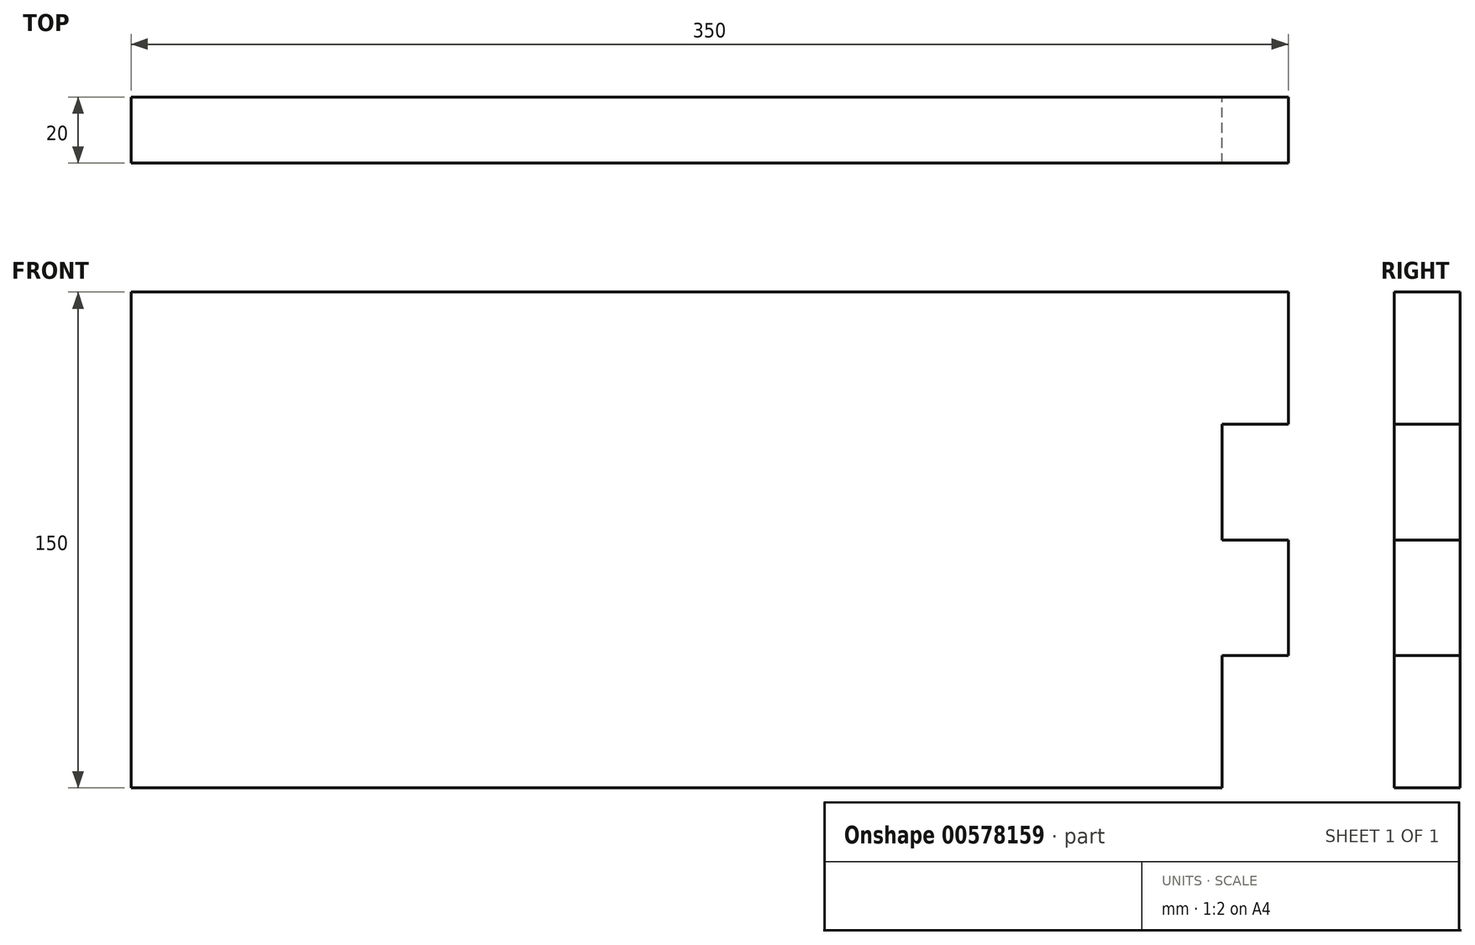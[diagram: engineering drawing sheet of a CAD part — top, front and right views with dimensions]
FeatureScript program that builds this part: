
annotation { "Feature Type Name" : "Feature", "Feature Type Description" : "" }
export const myFeature = defineFeature(function(context is Context, id is Id, definition is map)
    precondition{}
    {
        {
            var Q0;
            Q0=qCreatedBy(makeId("Front.planeOp"),FACE);
            var sketch = newSketch(context, id + "F0", { "sketchPlane" : qUnion([Q0])});
            skLineSegment(sketch, "E0.bottom", {"start": v(-20, 0) * mm, "end": v(-350, 0) * mm});
            skLineSegment(sketch, "E0.top", {"start": v(0, 150) * mm, "end": v(-350, 150) * mm});
            skLineSegment(sketch, "E0.left", {"start": v(0, 40) * mm, "end": v(0, 75) * mm});
            skLineSegment(sketch, "E0.right", {"start": v(-350, 0) * mm, "end": v(-350, 150) * mm});
            skLineSegment(sketch, "E1", {"start": v(-20, 110) * mm, "end": v(-20, 75) * mm});
            skLineSegment(sketch, "E2", {"start": v(0, 75) * mm, "end": v(-20, 75) * mm});
            skLineSegment(sketch, "E3", {"start": v(0, 110) * mm, "end": v(-20, 110) * mm});
            skLineSegment(sketch, "E4", {"start": v(0, 40) * mm, "end": v(-20, 40) * mm});
            skLineSegment(sketch, "E5.trimOffspring", {"start": v(0, 110) * mm, "end": v(0, 150) * mm});
            skPoint(sketch, "E6.orphan", {"position": v(0, 0) * mm});
            skLineSegment(sketch, "E7.trimOffspring", {"start": v(-20, 40) * mm, "end": v(-20, 0) * mm});
            skPoint(sketch, "E8.orphan", {"position": v(-20, 150) * mm});
            skSolve(sketch);
        }
        {
            var Q0;
            Q0=qSketchRegion(id+"F0",true);
            var Q1;
            Q1=makeQuery(id+"F0.imprint","IMPRINT",FACE,{"disambiguationData":[TD([[makeQuery(id+"F0.imprint","IMPRINT",EDGE,{"derivedFrom":sQuery(id+"F0.wireOp",EDGE,"E0.bottom")}),-1.0]])]});
            extrude(context, id + "F1", {"entities" : qUnion([Q0, Q1]), "depth" : 20 * mm, "offsetDistance" : 25.4 * mm});
        }
    });
